# Revit family: Mailboxes_4B+_Horizontal-Salsbury_Industries-Front_Load-6_Door_High_Units
name_source: partatom
category: Specialty Equipment
revit_build: Autodesk Revit 2016 (Build: 20150714_1515(x64)
units: mm (PartAtom-declared; Revit-internal decimal feet)

## family parameters
Always vertical = Yes
Cut with Voids When Loaded = No
Host = Wall
OmniClass Number = 23.40.90.14.11
OmniClass Title = Mail Boxes
Part Type = Normal
Room Calculation Point = No
Round Connector Dimension = Use Diameter
Shared = No

## types (4) — shared parameters
Above Finished Floor (AFF-Bottom of Door) = 28 "
Assembly Code = C1030910
Assembly Description = Mailboxes
Back Enclosure Material = Aluminum - Salsbury Finish - Anodized
Column Divider 2 = Yes
Depth = 16.5 "
Door Window Material = Plastic - Salsbury Finish - Clear
Height = 35.25 "
Installation Note = 4B+ Vertical Mailboxes are USPS approved for replacement installations.  For new construction, see Cluster Box Units and 4C Horizontal Mailboxes
Lock Material = Stainless Steel - Salsbury Finish -  Polished
Manufacturer = Salsbury Industries
MasterFormat Number = 10 55 00
MasterFormat Title = Postal Specialties
OmniClass 23 Number = 23.40.90.14.11
OmniClass 23 Title = Mail Boxes
Row Divider 4 = Yes
Row Divider 5 = Yes
Type Comments = 4B+ Horizontal Mailbox - Front Loading
URL = www.mailboxes.com
Version = 2.0 (05/31/18)
Visible Door Number = Yes

## per-type parameters (varying)
- 3630: Column Divider 1=Yes; Column Divider 3=Yes; Column Divider 4=Yes; Column Divider 5=Yes; Description=30 A Doors (29 Usable) - 6 Door High Unit; Door Slot L1=4B+ A and B Doors : A Door; Door Slot L10=4B+ A and B Doors : A Door; Door Slot L11=4B+ A and B Doors : A Door; Door Slot L12=4B+ A and B Doors : A Door; Door Slot L13=4B+ A and B Doors : A Door; Door Slot L14=4B+ A and B Doors : A Door; Door Slot L15=4B+ A and B Doors : A Door; Door Slot L16=4B+ A and B Doors : A Door; Door Slot L17=4B+ A and B Doors : A Door; Door Slot L18=4B+ A and B Doors : A Door; Door Slot L19=4B+ A and B Doors : A Door; Door Slot L2=4B+ A and B Doors : A Door; Door Slot L20=4B+ A and B Doors : A Door; Door Slot L21=4B+ A and B Doors : A Door; Door Slot L22=4B+ A and B Doors : A Door; Door Slot L23=4B+ A and B Doors : A Door; Door Slot L24=4B+ A and B Doors : A Door; Door Slot L25=4B+ A and B Doors : A Door; Door Slot L26=4B+ A and B Doors : A Door; Door Slot L27=4B+ A and B Doors : A Door; Door Slot L28=4B+ A and B Doors : A Door; Door Slot L29=4B+ A and B Doors : A Door; Door Slot L3=4B+ A and B Access Doors : A Door - Access; Door Slot L30=4B+ A and B Doors : A Door; Door Slot L4=4B+ A and B Doors : A Door; Door Slot L5=4B+ A and B Doors : A Door; Door Slot L6=4B+ A and B Doors : A Door; Door Slot L7=4B+ A and B Doors : A Door; Door Slot L8=4B+ A and B Doors : A Door; Door Slot L9=4B+ A and B Doors : A Door; Rough Opening Width=34.75 "; Width=35.75 "
- 3624: Column Divider 1=Yes; Column Divider 3=Yes; Column Divider 4=Yes; Column Divider 5=No; Description=24 A Doors (23 Usable) - 6 Door High Unit; Door Slot L1=4B+ A and B Doors : A Door; Door Slot L10=4B+ A and B Doors : A Door; Door Slot L11=4B+ A and B Doors : A Door; Door Slot L12=4B+ A and B Doors : A Door; Door Slot L13=4B+ A and B Doors : A Door; Door Slot L14=4B+ A and B Doors : A Door; Door Slot L15=4B+ A and B Doors : A Door; Door Slot L16=4B+ A and B Doors : A Door; Door Slot L17=4B+ A and B Doors : A Door; Door Slot L18=4B+ A and B Doors : A Door; Door Slot L19=4B+ A and B Doors : A Door; Door Slot L2=4B+ A and B Doors : A Door; Door Slot L20=4B+ A and B Doors : A Door; Door Slot L21=4B+ A and B Doors : A Door; Door Slot L22=4B+ A and B Doors : A Door; Door Slot L23=4B+ A and B Doors : A Door; Door Slot L24=4B+ A and B Doors : A Door; Door Slot L25=4B+ A and B Doors : None; Door Slot L26=4B+ A and B Doors : None; Door Slot L27=4B+ A and B Doors : None; Door Slot L28=4B+ A and B Doors : None; Door Slot L29=4B+ A and B Doors : None; Door Slot L3=4B+ A and B Access Doors : A Door - Access; Door Slot L30=4B+ A and B Doors : None; Door Slot L4=4B+ A and B Doors : A Door; Door Slot L5=4B+ A and B Doors : A Door; Door Slot L6=4B+ A and B Doors : A Door; Door Slot L7=4B+ A and B Doors : A Door; Door Slot L8=4B+ A and B Doors : A Door; Door Slot L9=4B+ A and B Doors : A Door; Rough Opening Width=28.25 "; Width=29.25 "
- 3612: Column Divider 1=No; Column Divider 3=No; Column Divider 4=Yes; Column Divider 5=No; Description=12 B Doors (11 Usable) - 6 Door High Unit; Door Slot L1=4B+ A and B Doors : None; Door Slot L10=4B+ A and B Doors : B Door; Door Slot L11=4B+ A and B Doors : B Door; Door Slot L12=4B+ A and B Doors : B Door; Door Slot L13=4B+ A and B Doors : None; Door Slot L14=4B+ A and B Doors : None; Door Slot L15=4B+ A and B Doors : None; Door Slot L16=4B+ A and B Doors : None; Door Slot L17=4B+ A and B Doors : None; Door Slot L18=4B+ A and B Doors : None; Door Slot L19=4B+ A and B Doors : B Door; Door Slot L2=4B+ A and B Doors : None; Door Slot L20=4B+ A and B Doors : B Door; Door Slot L21=4B+ A and B Doors : B Door; Door Slot L22=4B+ A and B Doors : B Door; Door Slot L23=4B+ A and B Doors : B Door; Door Slot L24=4B+ A and B Doors : B Door; Door Slot L25=4B+ A and B Doors : None; Door Slot L26=4B+ A and B Doors : None; Door Slot L27=4B+ A and B Doors : None; Door Slot L28=4B+ A and B Doors : None; Door Slot L29=4B+ A and B Doors : None; Door Slot L3=4B+ A and B Doors : None; Door Slot L30=4B+ A and B Doors : None; Door Slot L4=4B+ A and B Doors : None; Door Slot L5=4B+ A and B Doors : None; Door Slot L6=4B+ A and B Doors : None; Door Slot L7=4B+ A and B Doors : B Door; Door Slot L8=4B+ A and B Doors : B Door; Door Slot L9=4B+ A and B Access Doors : B Door - Access; Rough Opening Width=28.25 "; Width=29.25 "
- 3618: Column Divider 1=Yes; Column Divider 3=Yes; Column Divider 4=No; Column Divider 5=No; Description=18 A Doors (17 Usable) - 6 Door High Unit; Door Slot L1=4B+ A and B Doors : A Door; Door Slot L10=4B+ A and B Doors : A Door; Door Slot L11=4B+ A and B Doors : A Door; Door Slot L12=4B+ A and B Doors : A Door; Door Slot L13=4B+ A and B Doors : A Door; Door Slot L14=4B+ A and B Doors : A Door; Door Slot L15=4B+ A and B Doors : A Door; Door Slot L16=4B+ A and B Doors : A Door; Door Slot L17=4B+ A and B Doors : A Door; Door Slot L18=4B+ A and B Doors : A Door; Door Slot L19=4B+ A and B Doors : None; Door Slot L2=4B+ A and B Doors : A Door; Door Slot L20=4B+ A and B Doors : None; Door Slot L21=4B+ A and B Doors : None; Door Slot L22=4B+ A and B Doors : None; Door Slot L23=4B+ A and B Doors : None; Door Slot L24=4B+ A and B Doors : None; Door Slot L25=4B+ A and B Doors : None; Door Slot L26=4B+ A and B Doors : None; Door Slot L27=4B+ A and B Doors : None; Door Slot L28=4B+ A and B Doors : None; Door Slot L29=4B+ A and B Doors : None; Door Slot L3=4B+ A and B Access Doors : A Door - Access; Door Slot L30=4B+ A and B Doors : None; Door Slot L4=4B+ A and B Doors : A Door; Door Slot L5=4B+ A and B Doors : A Door; Door Slot L6=4B+ A and B Doors : A Door; Door Slot L7=4B+ A and B Doors : A Door; Door Slot L8=4B+ A and B Doors : A Door; Door Slot L9=4B+ A and B Doors : A Door; Rough Opening Width=21.75 "; Width=22.75 "

note: column(s) folded — value = type name in every type: Model

## geometry (parser evidence)
native form markers: Sweep x7
no freeform markers — native parametric forms only
